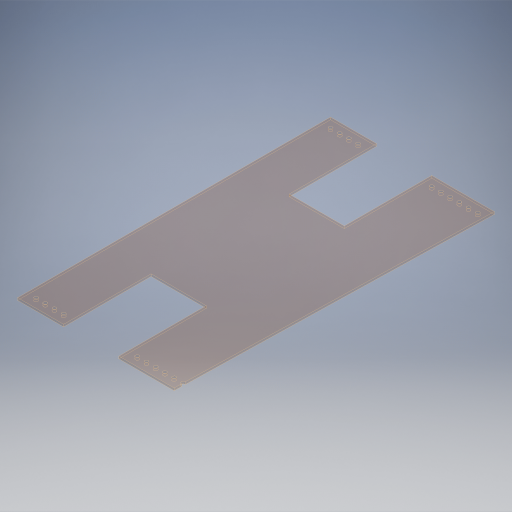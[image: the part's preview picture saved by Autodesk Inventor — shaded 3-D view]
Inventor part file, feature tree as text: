
AUTODESK INVENTOR PART (.ipt)
format: ipt  version: 2024.2 (Build 282272000, 272)  size: 404,992 bytes
history: native  units: in
note: dims shown in document units (in); Inventor stores cm internally (conversion verified against a paired STEP export)
features: extrude x4, sketch x3, projected_geometry x2
ambient origin geometry x8: Origin, YZ Plane, XZ Plane, XY Plane, X Axis, Y Axis, Z Axis, Center Point
bodies: Solid1 (feature_tree)
feature tree (9):
  extrude  "Extrusion1"  Depth=17.0in
  sketch  "Sketch2"  dims[d2=2.5in d3=4.75in]
  extrude  "Extrusion2"  Depth=4.75in
  extrude  "Extrusion3"  Depth=2.5in
  extrude  "Extrusion4"  Depth=4.75in
  sketch  "Sketch1"  dims[d0=23.748in d1=17.0in]
  projected_geometry  "Projected Loop1"
  sketch  "Sketch3"  dims[d4=3.0in d5=2.5in d6=4.75in d7=3.0in d8=4.75in d9=4.75in d10=0.196in d11=0.5in d12=0.5in d13=1.5748in d15=0.5in d16=0.3937in d18=1.0in d20=0.196in d21=0.5in d22=0.5in d23=3.1496in d25=0.5in d26=0.3937in d28=1.0in d30=0.5in d31=0.25in d32=0.0in d33=8.5in d34=1.0in d35=0.0in d36=1.0in d37=0.0in d38=0.125in d39=0.0in]
  projected_geometry  "Projected Loop2"
